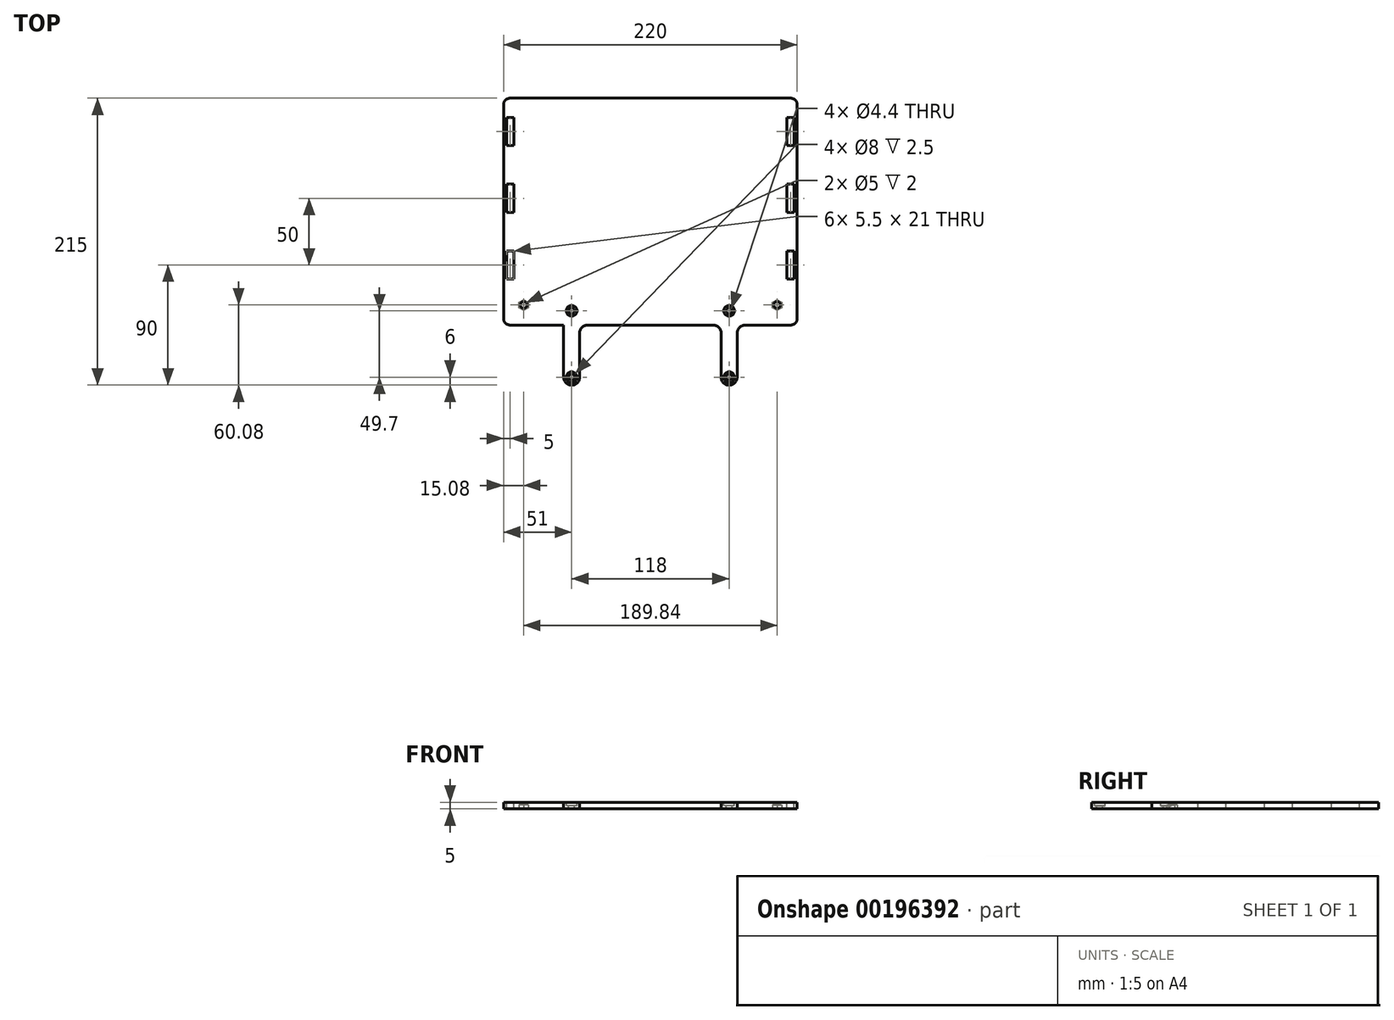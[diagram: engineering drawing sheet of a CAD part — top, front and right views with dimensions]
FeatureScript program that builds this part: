
annotation { "Feature Type Name" : "Feature", "Feature Type Description" : "" }
export const myFeature = defineFeature(function(context is Context, id is Id, definition is map)
    precondition{}
    {
        {
            var Q0;
            Q0=qCreatedBy(makeId("Top.planeOp"),FACE);
            var sketch = newSketch(context, id + "F0", { "sketchPlane" : qUnion([Q0])});
            skLineSegment(sketch, "E0.bottom", {"start": v(100, 75) * mm, "end": v(-100, 75) * mm});
            skLineSegment(sketch, "E0.top", {"start": v(100, -75) * mm, "end": v(-100, -75) * mm});
            skLineSegment(sketch, "E0.left", {"start": v(100, 75) * mm, "end": v(100, -75) * mm});
            skLineSegment(sketch, "E0.right", {"start": v(-100, 75) * mm, "end": v(-100, -75) * mm});
            skPoint(sketch, "E0.middle", {"position": v(0, 0) * mm});
            skLineSegment(sketch, "E1.bottom", {"start": v(110, 85) * mm, "end": v(-110, 85) * mm});
            skLineSegment(sketch, "E1.top", {"start": v(110, -85) * mm, "end": v(-110, -85) * mm});
            skLineSegment(sketch, "E1.left", {"start": v(110, 85) * mm, "end": v(110, -85) * mm});
            skLineSegment(sketch, "E1.right", {"start": v(-110, 85) * mm, "end": v(-110, -85) * mm});
            skSolve(sketch);
        }
        {
            var Q0;
            Q0=makeQuery(id+"F0.imprint","IMPRINT",FACE,{"disambiguationData":[TD([[makeQuery(id+"F0.imprint","IMPRINT",EDGE,{"derivedFrom":sQuery(id+"F0.wireOp",EDGE,"E0.bottom")}),-1.0]])]});
            var Q1;
            Q1=makeQuery(id+"F0.imprint","IMPRINT",FACE,{"disambiguationData":[TD([[makeQuery(id+"F0.imprint","IMPRINT",EDGE,{"derivedFrom":sQuery(id+"F0.wireOp",EDGE,"E0.bottom")}),1.0]])]});
            extrude(context, id + "F1", {"entities" : qUnion([Q0, Q1]), "depth" : 5 * mm});
        }
        {
            var Q0;
            Q0=makeQuery(id+"F1.opExtrude","CAP_FACE",FACE,{"disambiguationData":[OSD([sQuery(id+"F0.wireOp",EDGE,"E1.bottom"),sQuery(id+"F0.wireOp",EDGE,"E1.top"),sQuery(id+"F0.wireOp",EDGE,"E1.left"),sQuery(id+"F0.wireOp",EDGE,"E1.right")])],"isStart":false});
            var sketch = newSketch(context, id + "F2", { "sketchPlane" : qUnion([Q0])});
            skLineSegment(sketch, "E2.bottom", {"start": v(-102.25, 70.5) * mm, "end": v(-107.75, 70.5) * mm});
            skLineSegment(sketch, "E2.top", {"start": v(-102.25, 49.5) * mm, "end": v(-107.75, 49.5) * mm});
            skLineSegment(sketch, "E2.left", {"start": v(-102.25, 70.5) * mm, "end": v(-102.25, 49.5) * mm});
            skLineSegment(sketch, "E2.right", {"start": v(-107.75, 70.5) * mm, "end": v(-107.75, 49.5) * mm});
            skPoint(sketch, "E2.middle", {"position": v(-105, 60) * mm});
            skPoint(sketch, "E3.0.1.0", {"position": v(-105, 10) * mm});
            skLineSegment(sketch, "E3.0.1.1", {"start": v(-102.25, 20.5) * mm, "end": v(-102.25, -0.5) * mm});
            skLineSegment(sketch, "E3.0.1.2", {"start": v(-107.75, 20.5) * mm, "end": v(-107.75, -0.5) * mm});
            skLineSegment(sketch, "E3.0.1.3", {"start": v(-102.25, 20.5) * mm, "end": v(-107.75, 20.5) * mm});
            skLineSegment(sketch, "E3.0.1.4", {"start": v(-102.25, -0.5) * mm, "end": v(-107.75, -0.5) * mm});
            skPoint(sketch, "E3.0.2.0", {"position": v(-105, -40) * mm});
            skLineSegment(sketch, "E3.0.2.1", {"start": v(-102.25, -29.5) * mm, "end": v(-102.25, -50.5) * mm});
            skLineSegment(sketch, "E3.0.2.2", {"start": v(-107.75, -29.5) * mm, "end": v(-107.75, -50.5) * mm});
            skLineSegment(sketch, "E3.0.2.3", {"start": v(-102.25, -29.5) * mm, "end": v(-107.75, -29.5) * mm});
            skLineSegment(sketch, "E3.0.2.4", {"start": v(-102.25, -50.5) * mm, "end": v(-107.75, -50.5) * mm});
            skPoint(sketch, "E3.1.0.0", {"position": v(105, 60) * mm});
            skLineSegment(sketch, "E3.1.0.1", {"start": v(107.75, 70.5) * mm, "end": v(107.75, 49.5) * mm});
            skLineSegment(sketch, "E3.1.0.2", {"start": v(102.25, 70.5) * mm, "end": v(102.25, 49.5) * mm});
            skLineSegment(sketch, "E3.1.0.3", {"start": v(107.75, 70.5) * mm, "end": v(102.25, 70.5) * mm});
            skLineSegment(sketch, "E3.1.0.4", {"start": v(107.75, 49.5) * mm, "end": v(102.25, 49.5) * mm});
            skPoint(sketch, "E3.1.1.0", {"position": v(105, 10) * mm});
            skLineSegment(sketch, "E3.1.1.1", {"start": v(107.75, 20.5) * mm, "end": v(107.75, -0.5) * mm});
            skLineSegment(sketch, "E3.1.1.2", {"start": v(102.25, 20.5) * mm, "end": v(102.25, -0.5) * mm});
            skLineSegment(sketch, "E3.1.1.3", {"start": v(107.75, 20.5) * mm, "end": v(102.25, 20.5) * mm});
            skLineSegment(sketch, "E3.1.1.4", {"start": v(107.75, -0.5) * mm, "end": v(102.25, -0.5) * mm});
            skPoint(sketch, "E3.1.2.0", {"position": v(105, -40) * mm});
            skLineSegment(sketch, "E3.1.2.1", {"start": v(107.75, -29.5) * mm, "end": v(107.75, -50.5) * mm});
            skLineSegment(sketch, "E3.1.2.2", {"start": v(102.25, -29.5) * mm, "end": v(102.25, -50.5) * mm});
            skLineSegment(sketch, "E3.1.2.3", {"start": v(107.75, -29.5) * mm, "end": v(102.25, -29.5) * mm});
            skLineSegment(sketch, "E3.1.2.4", {"start": v(107.75, -50.5) * mm, "end": v(102.25, -50.5) * mm});
            skLineSegment(sketch, "E3.direction1", {"start": v(-107.75, 49.5) * mm, "end": v(102.25, 49.5) * mm, "construction": true});
            skLineSegment(sketch, "E3.direction2", {"start": v(-107.75, 49.5) * mm, "end": v(-107.75, -0.5) * mm, "construction": true});
            skSolve(sketch);
        }
        {
            var Q0;
            Q0 = qSketchRegion(id + "F2", true);
            extrude(context, id + "F3", {"entities" : qUnion([Q0]), "operationType" : NewBodyOperationType.REMOVE, "oppositeDirection" : true, "depth" : 25 * mm});
        }
        {
            var Q0;
            Q0=makeQuery(id+"F1.opExtrude","SWEPT_FACE",FACE,{"disambiguationData":[OSD([sQuery(id+"F0.wireOp",EDGE,"E1.top")])]});
            var sketch = newSketch(context, id + "F4", { "sketchPlane" : qUnion([Q0])});
            skLineSegment(sketch, "E4.bottom", {"start": v(-65, 5) * mm, "end": v(-53, 5) * mm});
            skLineSegment(sketch, "E4.top", {"start": v(-65, 0) * mm, "end": v(-53, 0) * mm});
            skLineSegment(sketch, "E4.left", {"start": v(-65, 5) * mm, "end": v(-65, 0) * mm});
            skLineSegment(sketch, "E4.right", {"start": v(-53, 5) * mm, "end": v(-53, 0) * mm});
            skLineSegment(sketch, "E5.1.0.0", {"start": v(53, 0) * mm, "end": v(65, 0) * mm});
            skLineSegment(sketch, "E5.1.0.1", {"start": v(53, 5) * mm, "end": v(65, 5) * mm});
            skLineSegment(sketch, "E5.1.0.2", {"start": v(53, 5) * mm, "end": v(53, 0) * mm});
            skLineSegment(sketch, "E5.1.0.3", {"start": v(65, 5) * mm, "end": v(65, 0) * mm});
            skLineSegment(sketch, "E5.2.0.0", {"start": v(171, 0) * mm, "end": v(183, 0) * mm});
            skLineSegment(sketch, "E5.2.0.1", {"start": v(171, 5) * mm, "end": v(183, 5) * mm});
            skLineSegment(sketch, "E5.2.0.2", {"start": v(171, 5) * mm, "end": v(171, 0) * mm});
            skLineSegment(sketch, "E5.2.0.3", {"start": v(183, 5) * mm, "end": v(183, 0) * mm});
            skLineSegment(sketch, "E5.direction1", {"start": v(-65, 0) * mm, "end": v(53, 0) * mm, "construction": true});
            skSolve(sketch);
        }
        {
            var Q0;
            Q0=makeQuery(id+"F4.imprint","IMPRINT",FACE,{"disambiguationData":[TD([[makeQuery(id+"F4.imprint","IMPRINT",EDGE,{"derivedFrom":sQuery(id+"F4.wireOp",EDGE,"E5.1.0.0")}),-1.0]])]});
            var Q1;
            Q1=makeQuery(id+"F4.imprint","IMPRINT",FACE,{"disambiguationData":[TD([[makeQuery(id+"F4.imprint","IMPRINT",EDGE,{"derivedFrom":sQuery(id+"F4.wireOp",EDGE,"E4.bottom")}),1.0]])]});
            extrude(context, id + "F5", {"entities" : qUnion([Q0, Q1]), "operationType" : NewBodyOperationType.ADD, "depth" : 45 * mm});
        }
        {
            var Q0;
            Q0=makeQuery(id+"F5.boolean.opBoolean","MERGE",FACE,{"derivedFrom":[makeQuery(id+"F1.opExtrude","CAP_FACE",FACE,{"disambiguationData":[OSD([sQuery(id+"F0.wireOp",EDGE,"E1.bottom"),sQuery(id+"F0.wireOp",EDGE,"E1.top"),sQuery(id+"F0.wireOp",EDGE,"E1.left"),sQuery(id+"F0.wireOp",EDGE,"E1.right")])],"isStart":false}),makeQuery(id+"F5.opExtrude","SWEPT_FACE",FACE,{"disambiguationData":[OSD([sQuery(id+"F4.wireOp",EDGE,"E4.bottom")])]}),makeQuery(id+"F5.opExtrude","SWEPT_FACE",FACE,{"disambiguationData":[OSD([sQuery(id+"F4.wireOp",EDGE,"E5.1.0.1")])]})]});
            var sketch = newSketch(context, id + "F6", { "sketchPlane" : qUnion([Q0])});
            skCircle(sketch, "E6", {"center": v(-59, -124) * mm, "radius": 2.2 * mm});
            skCircle(sketch, "E7.0.1.0", {"center": v(-59, -74.3) * mm, "radius": 2.2 * mm});
            skCircle(sketch, "E7.1.0.0", {"center": v(59, -124) * mm, "radius": 2.2 * mm});
            skCircle(sketch, "E7.1.1.0", {"center": v(59, -74.3) * mm, "radius": 2.2 * mm});
            skLineSegment(sketch, "E7.direction1", {"start": v(-59, -124) * mm, "end": v(59, -124) * mm, "construction": true});
            skLineSegment(sketch, "E7.direction2", {"start": v(-59, -124) * mm, "end": v(-59, -74.3) * mm, "construction": true});
            skSolve(sketch);
        }
        {
            var Q0;
            Q0=makeQuery(id+"F6.imprint","IMPRINT",FACE,{"disambiguationData":[TD([[makeQuery(id+"F6.imprint","IMPRINT",EDGE,{"derivedFrom":sQuery(id+"F6.wireOp",EDGE,"E7.0.1.0")}),1.0]])]});
            var Q1;
            Q1=makeQuery(id+"F6.imprint","IMPRINT",FACE,{"disambiguationData":[TD([[makeQuery(id+"F6.imprint","IMPRINT",EDGE,{"derivedFrom":sQuery(id+"F6.wireOp",EDGE,"E6")}),1.0]])]});
            var Q2;
            Q2=makeQuery(id+"F6.imprint","IMPRINT",FACE,{"disambiguationData":[TD([[makeQuery(id+"F6.imprint","IMPRINT",EDGE,{"derivedFrom":sQuery(id+"F6.wireOp",EDGE,"E7.1.1.0")}),1.0]])]});
            var Q3;
            Q3=makeQuery(id+"F6.imprint","IMPRINT",FACE,{"disambiguationData":[TD([[makeQuery(id+"F6.imprint","IMPRINT",EDGE,{"derivedFrom":sQuery(id+"F6.wireOp",EDGE,"E7.1.0.0")}),1.0]])]});
            extrude(context, id + "F7", {"entities" : qUnion([Q0, Q1, Q2, Q3]), "operationType" : NewBodyOperationType.REMOVE, "oppositeDirection" : true, "depth" : 25 * mm});
        }
        {
            var Q0;
            Q0=makeQuery(id+"F5.opExtrude","CAP_EDGE",EDGE,{"disambiguationData":[OSD([sQuery(id+"F4.wireOp",EDGE,"E4.left")])],"isStart":false});
            var Q1;
            Q1=makeQuery(id+"F5.opExtrude","CAP_EDGE",EDGE,{"disambiguationData":[OSD([sQuery(id+"F4.wireOp",EDGE,"E4.right")])],"isStart":false});
            var Q2;
            Q2=makeQuery(id+"F5.opExtrude","CAP_EDGE",EDGE,{"disambiguationData":[OSD([sQuery(id+"F4.wireOp",EDGE,"E5.1.0.2")])],"isStart":false});
            var Q3;
            Q3=makeQuery(id+"F5.opExtrude","CAP_EDGE",EDGE,{"disambiguationData":[OSD([sQuery(id+"F4.wireOp",EDGE,"E5.1.0.3")])],"isStart":false});
            fillet(context, id + "F8", {"entities" : qUnion([Q0, Q1, Q2, Q3]), "radius" : 6 * mm, "tangentPropagation" : true, "allowEdgeOverflow" : false});
        }
        {
            var Q0;
            Q0=makeQuery(id+"F5.opExtrude","CAP_EDGE",EDGE,{"disambiguationData":[OSD([sQuery(id+"F4.wireOp",EDGE,"E4.left")])],"isStart":true});
            var Q1;
            Q1=makeQuery(id+"F5.opExtrude","CAP_EDGE",EDGE,{"disambiguationData":[OSD([sQuery(id+"F4.wireOp",EDGE,"E4.right")])],"isStart":true});
            var Q2;
            Q2=makeQuery(id+"F5.opExtrude","CAP_EDGE",EDGE,{"disambiguationData":[OSD([sQuery(id+"F4.wireOp",EDGE,"E5.1.0.2")])],"isStart":true});
            var Q3;
            Q3=makeQuery(id+"F5.opExtrude","CAP_EDGE",EDGE,{"disambiguationData":[OSD([sQuery(id+"F4.wireOp",EDGE,"E5.1.0.3")])],"isStart":true});
            fillet(context, id + "F9", {"entities" : qUnion([Q0, Q1, Q2, Q3]), "radius" : 6 * mm, "tangentPropagation" : true, "allowEdgeOverflow" : false});
        }
        {
            var Q0;
            Q0=makeQuery(id+"F5.boolean.opBoolean","MERGE",FACE,{"derivedFrom":[makeQuery(id+"F1.opExtrude","CAP_FACE",FACE,{"disambiguationData":[OSD([sQuery(id+"F0.wireOp",EDGE,"E1.bottom"),sQuery(id+"F0.wireOp",EDGE,"E1.top"),sQuery(id+"F0.wireOp",EDGE,"E1.left"),sQuery(id+"F0.wireOp",EDGE,"E1.right")])],"isStart":false}),makeQuery(id+"F5.opExtrude","SWEPT_FACE",FACE,{"disambiguationData":[OSD([sQuery(id+"F4.wireOp",EDGE,"E4.bottom")])]}),makeQuery(id+"F5.opExtrude","SWEPT_FACE",FACE,{"disambiguationData":[OSD([sQuery(id+"F4.wireOp",EDGE,"E5.1.0.1")])]})]});
            var sketch = newSketch(context, id + "F10", { "sketchPlane" : qUnion([Q0])});
            skCircle(sketch, "E8", {"center": v(-59, -124) * mm, "radius": 4 * mm});
            skCircle(sketch, "E9", {"center": v(-59, -74.3) * mm, "radius": 4 * mm});
            skCircle(sketch, "E10", {"center": v(59, -74.3) * mm, "radius": 4 * mm});
            skCircle(sketch, "E11", {"center": v(59, -124) * mm, "radius": 4 * mm});
            skSolve(sketch);
        }
        {
            var Q0;
            Q0 = qSketchRegion(id + "F10", true);
            extrude(context, id + "F11", {"entities" : qUnion([Q0]), "operationType" : NewBodyOperationType.REMOVE, "oppositeDirection" : true, "depth" : 2.5 * mm});
        }
        {
            var Q0;
            Q0=makeQuery(id+"F5.boolean.opBoolean","MERGE",FACE,{"derivedFrom":[makeQuery(id+"F1.opExtrude","CAP_FACE",FACE,{"disambiguationData":[OSD([sQuery(id+"F0.wireOp",EDGE,"E1.bottom"),sQuery(id+"F0.wireOp",EDGE,"E1.top"),sQuery(id+"F0.wireOp",EDGE,"E1.left"),sQuery(id+"F0.wireOp",EDGE,"E1.right")])],"isStart":false}),makeQuery(id+"F5.opExtrude","SWEPT_FACE",FACE,{"disambiguationData":[OSD([sQuery(id+"F4.wireOp",EDGE,"E4.bottom")])]}),makeQuery(id+"F5.opExtrude","SWEPT_FACE",FACE,{"disambiguationData":[OSD([sQuery(id+"F4.wireOp",EDGE,"E5.1.0.1")])]})]});
            var sketch = newSketch(context, id + "F12", { "sketchPlane" : qUnion([Q0])});
            skCircle(sketch, "E12", {"center": v(94.92, -69.92) * mm, "radius": 2.5 * mm});
            skCircle(sketch, "E13", {"center": v(-94.92, -69.92) * mm, "radius": 2.5 * mm});
            skSolve(sketch);
        }
        {
            var Q0;
            Q0=makeQuery(id+"F1.opExtrude","SWEPT_EDGE",EDGE,{"disambiguationData":[OSD([sQuery(id+"F0.wireOp",EDGE,"E1.top"),sQuery(id+"F0.wireOp",EDGE,"E1.right")])]});
            var Q1;
            Q1=makeQuery(id+"F1.opExtrude","SWEPT_EDGE",EDGE,{"disambiguationData":[OSD([sQuery(id+"F0.wireOp",EDGE,"E1.top"),sQuery(id+"F0.wireOp",EDGE,"E1.left")])]});
            var Q2;
            Q2=makeQuery(id+"F1.opExtrude","SWEPT_EDGE",EDGE,{"disambiguationData":[OSD([sQuery(id+"F0.wireOp",EDGE,"E1.bottom"),sQuery(id+"F0.wireOp",EDGE,"E1.left")])]});
            var Q3;
            Q3=makeQuery(id+"F1.opExtrude","SWEPT_EDGE",EDGE,{"disambiguationData":[OSD([sQuery(id+"F0.wireOp",EDGE,"E1.bottom"),sQuery(id+"F0.wireOp",EDGE,"E1.right")])]});
            fillet(context, id + "F13", {"entities" : qUnion([Q0, Q1, Q2, Q3]), "radius" : 5 * mm, "tangentPropagation" : true, "allowEdgeOverflow" : false});
        }
        {
            var Q0;
            Q0=makeQuery(id+"F0.imprint","IMPRINT",FACE,{"disambiguationData":[TD([[makeQuery(id+"F0.imprint","IMPRINT",EDGE,{"derivedFrom":sQuery(id+"F0.wireOp",EDGE,"E0.bottom")}),-1.0]])]});
            var sketch = newSketch(context, id + "F14", { "sketchPlane" : qUnion([Q0])});
            skCircle(sketch, "E14.cCircle", {"center": v(-94.92, -69.92) * mm, "radius": 3.5 * mm, "construction": true});
            skLineSegment(sketch, "E14.0", {"start": v(-98.42, -71.94) * mm, "end": v(-98.42, -67.9) * mm});
            skLineSegment(sketch, "E14.1", {"start": v(-98.42, -67.9) * mm, "end": v(-94.92, -65.88) * mm});
            skLineSegment(sketch, "E14.2", {"start": v(-94.92, -65.88) * mm, "end": v(-91.42, -67.9) * mm});
            skLineSegment(sketch, "E14.3", {"start": v(-91.42, -67.9) * mm, "end": v(-91.42, -71.94) * mm});
            skLineSegment(sketch, "E14.4", {"start": v(-91.42, -71.94) * mm, "end": v(-94.92, -73.96) * mm});
            skLineSegment(sketch, "E14.5", {"start": v(-94.92, -73.96) * mm, "end": v(-98.42, -71.94) * mm});
            skPoint(sketch, "E14.0.midPoint", {"position": v(-98.42, -69.92) * mm});
            skCircle(sketch, "E15.cCircle", {"center": v(94.92, -69.92) * mm, "radius": 3.5 * mm, "construction": true});
            skLineSegment(sketch, "E15.0", {"start": v(98.42, -67.9) * mm, "end": v(98.42, -71.94) * mm});
            skLineSegment(sketch, "E15.1", {"start": v(98.42, -71.94) * mm, "end": v(94.92, -73.96) * mm});
            skLineSegment(sketch, "E15.2", {"start": v(94.92, -73.96) * mm, "end": v(91.42, -71.94) * mm});
            skLineSegment(sketch, "E15.3", {"start": v(91.42, -71.94) * mm, "end": v(91.42, -67.9) * mm});
            skLineSegment(sketch, "E15.4", {"start": v(91.42, -67.9) * mm, "end": v(94.92, -65.88) * mm});
            skLineSegment(sketch, "E15.5", {"start": v(94.92, -65.88) * mm, "end": v(98.42, -67.9) * mm});
            skPoint(sketch, "E15.0.midPoint", {"position": v(98.42, -69.92) * mm});
            skSolve(sketch);
        }
        {
            var Q0;
            Q0 = qSketchRegion(id + "F14", true);
            extrude(context, id + "F15", {"entities" : qUnion([Q0]), "operationType" : NewBodyOperationType.REMOVE, "depth" : 3 * mm});
        }
        {
            var Q0;
            Q0 = qSketchRegion(id + "F12", true);
            extrude(context, id + "F16", {"entities" : qUnion([Q0]), "operationType" : NewBodyOperationType.REMOVE, "oppositeDirection" : true, "depth" : 3 * mm});
        }
    });
